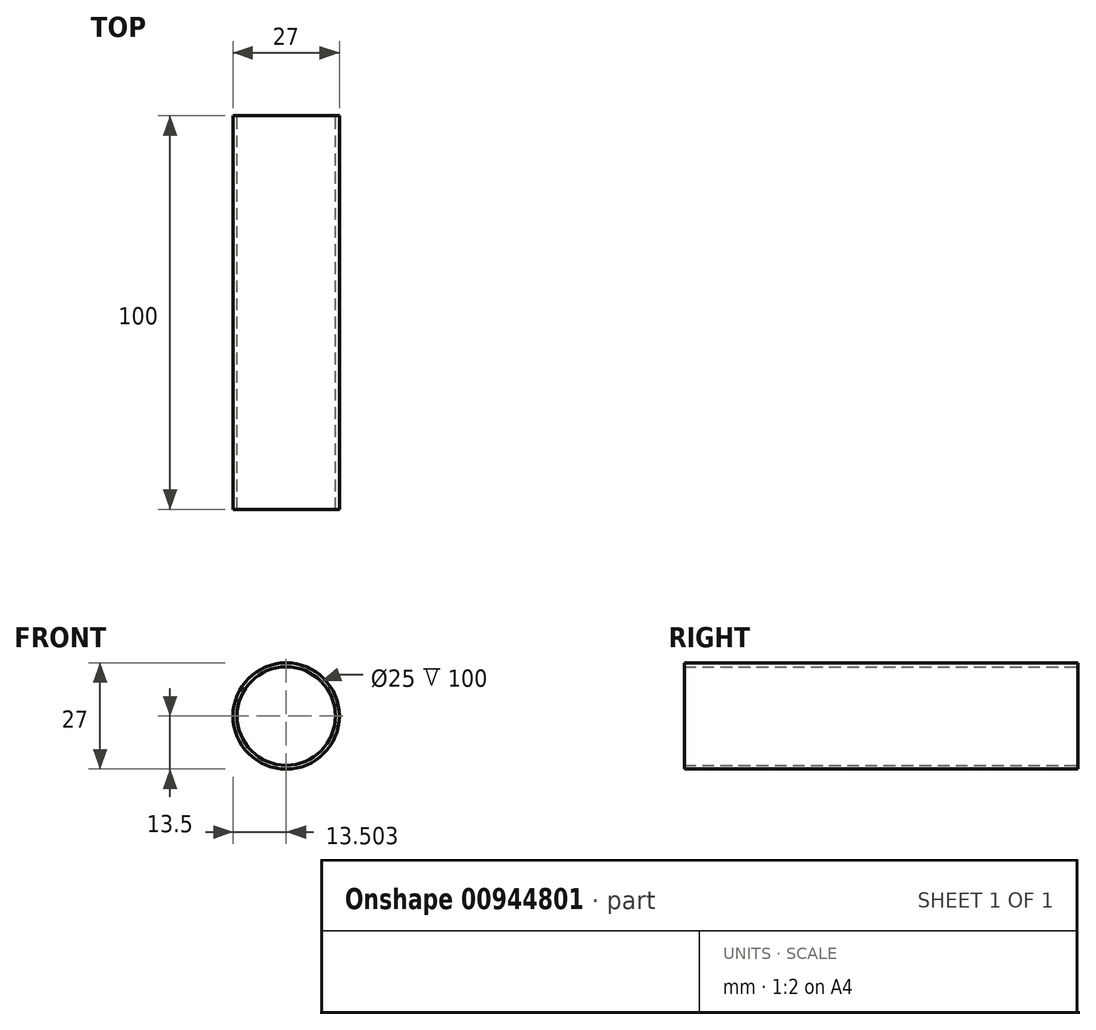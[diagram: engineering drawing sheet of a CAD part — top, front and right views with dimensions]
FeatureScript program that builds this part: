
annotation { "Feature Type Name" : "Feature", "Feature Type Description" : "" }
export const myFeature = defineFeature(function(context is Context, id is Id, definition is map)
    precondition{}
    {
        {
            var Q0;
            Q0=qCreatedBy(makeId("Front.planeOp"),FACE);
            var sketch = newSketch(context, id + "F0", { "sketchPlane" : qUnion([Q0])});
            skCircle(sketch, "E0", {"center": v(2.35, 0) * mm, "radius": 12.5 * mm});
            skCircle(sketch, "E1", {"center": v(2.35, 0) * mm, "radius": 13.5 * mm});
            skSolve(sketch);
        }
        {
            var Q0;
            Q0 = qSketchRegion(id + "F0", true);
            extrude(context, id + "F1", {"entities" : qUnion([Q0]), "depth" : 100 * mm, "offsetDistance" : 25 * mm});
        }
    });
